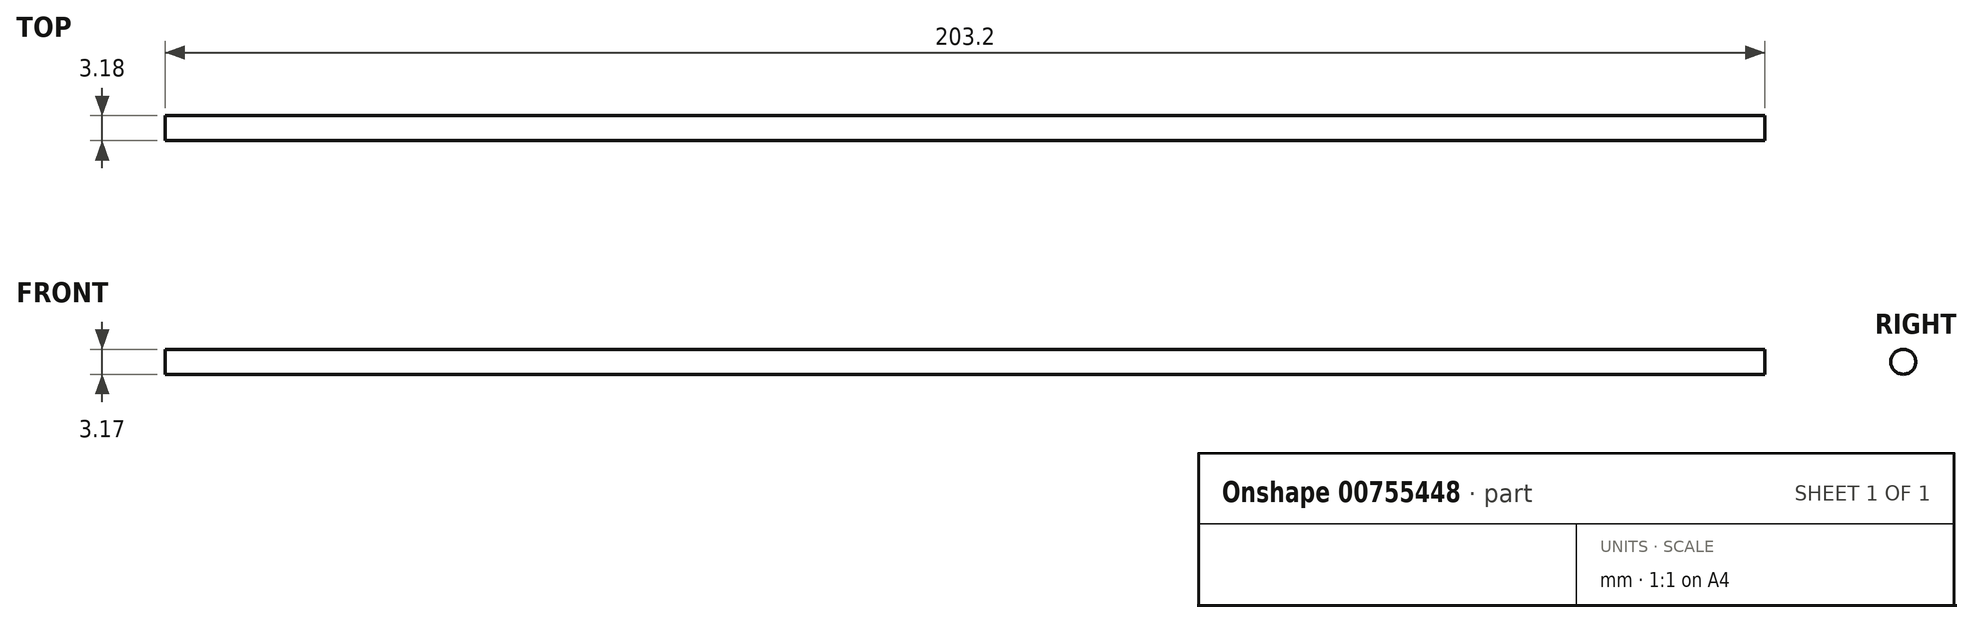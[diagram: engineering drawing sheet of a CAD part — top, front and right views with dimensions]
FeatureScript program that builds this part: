
annotation { "Feature Type Name" : "Feature", "Feature Type Description" : "" }
export const myFeature = defineFeature(function(context is Context, id is Id, definition is map)
    precondition{}
    {
        {
            var Q0;
            Q0=qCreatedBy(makeId("Right.planeOp"),FACE);
            var sketch = newSketch(context, id + "F0", { "sketchPlane" : qUnion([Q0])});
            skCircle(sketch, "E0", {"center": v(37.78, 37.28) * mm, "radius": 1.59 * mm});
            skSolve(sketch);
        }
        {
            var Q0;
            Q0 = qSketchRegion(id + "F0", true);
            extrude(context, id + "F1", {"entities" : qUnion([Q0]), "depth" : 203.2 * mm, "offsetDistance" : 25.4 * mm});
        }
    });
